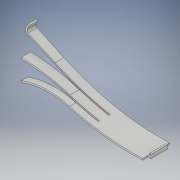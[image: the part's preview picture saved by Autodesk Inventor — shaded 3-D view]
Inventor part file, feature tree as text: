
AUTODESK INVENTOR PART (.ipt)
format: ipt  version: 2018.3 (Build 223284000, 284)  size: 201,728 bytes
history: native  units: in
note: dims shown in document units (in); Inventor stores cm internally (conversion verified against a paired STEP export)
features: extrude x5, sketch x3, plane x3
ambient origin geometry x8: Origin, YZ Plane, XZ Plane, XY Plane, X Axis, Y Axis, Z Axis, Center Point
bodies: Solid1 (feature_tree)
feature tree (11):
  sketch  "Sketch1"  dims[d3=9.0in d4=0.25in]
  extrude  "Extrusion1"  Depth=0.25in
  plane  "Work Plane6"
  extrude  "Extrusion2"  Depth=0.031in
  extrude  "Extrusion3"  Depth=0.015in
  plane  "Work Plane7"
  extrude  "Extrusion4"  Depth=1.06in
  plane  "Work Plane8"
  extrude  "Extrusion5"  Depth=0.532in TaperAngle=0.0deg
  sketch  "Sketch3"  dims[d5=0.031in d6=0.031in]
  sketch  "Sketch6"  dims[d7=0.078in d8=0.015in d14=1.06in d15=0.532in d16=0.0in d17=0.185in d18=0.0in d19=2.598in d20=0.384in d21=7.0in d28=0.135in d29=2.439in d30=3.0in d31=0.122in d32=0.0in d34=-0.147in d35=0.025in d42=0.66in d43=2.687in d44=0.031in d45=0.031in d46=0.155in d47=0.04in d50=0.0314in d51=0.175in d52=0.0in d53=0.0in d54=0.33in d55=0.165in d56=0.058in d57=0.058in d58=0.101in d59=0.122in d60=0.0in]
